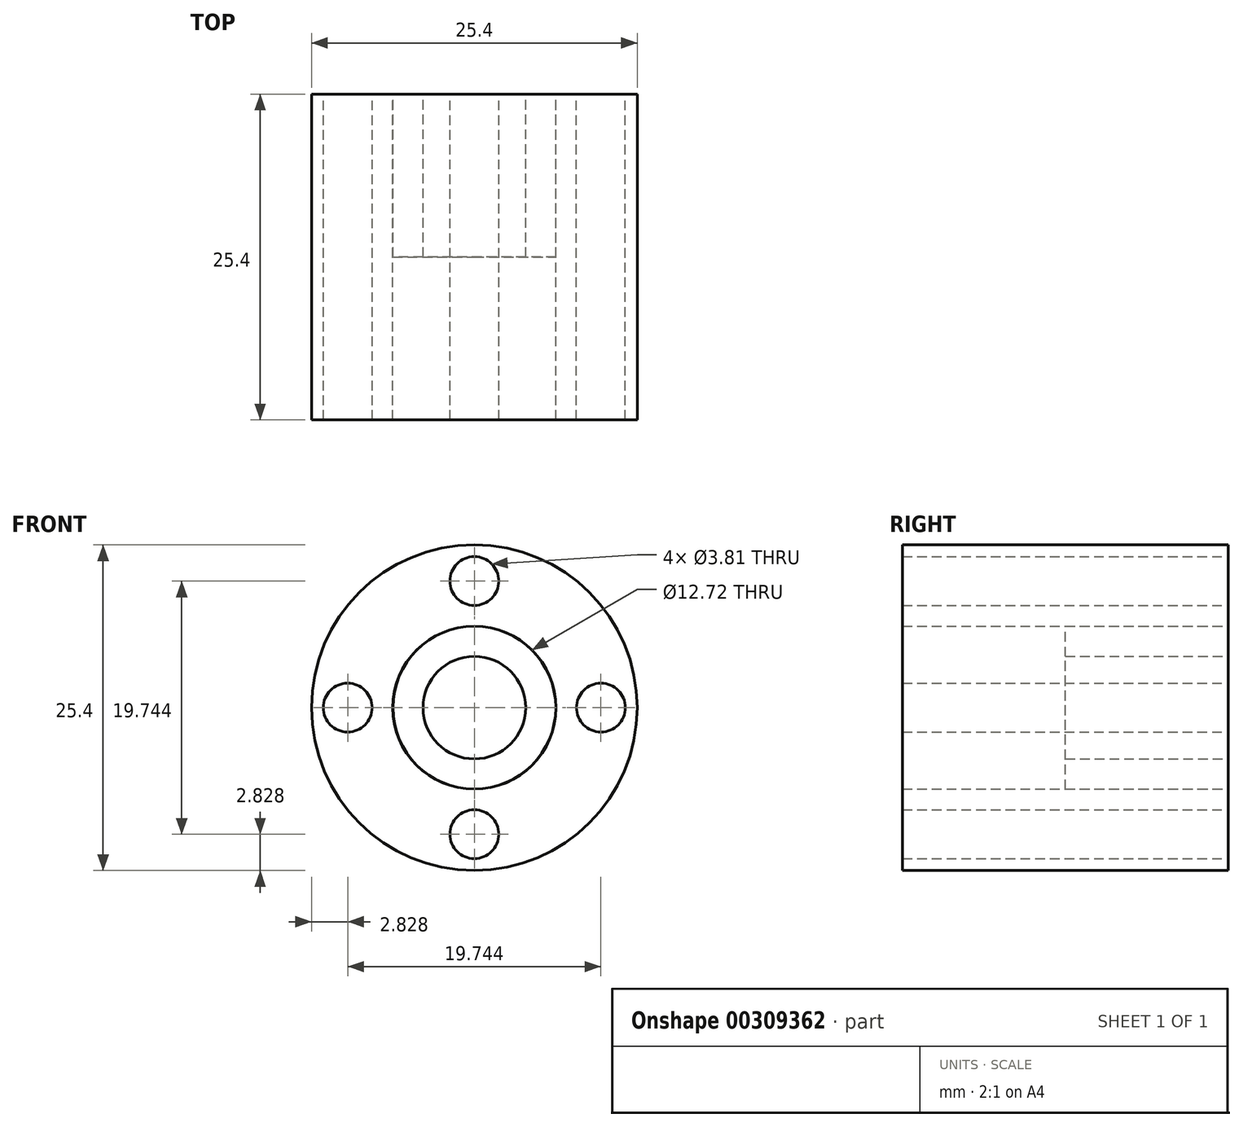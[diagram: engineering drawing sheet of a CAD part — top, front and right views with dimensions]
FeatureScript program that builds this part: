
annotation { "Feature Type Name" : "Feature", "Feature Type Description" : "" }
export const myFeature = defineFeature(function(context is Context, id is Id, definition is map)
    precondition{}
    {
        {
            var Q0;
            Q0=qCreatedBy(makeId("Front.planeOp"),FACE);
            var sketch = newSketch(context, id + "F0", { "sketchPlane" : qUnion([Q0])});
            skCircle(sketch, "E0", {"center": v(0, 0) * mm, "radius": 12.7 * mm});
            skCircle(sketch, "E1", {"center": v(0, 0) * mm, "radius": 6.36 * mm});
            skCircle(sketch, "E2", {"center": v(0, 0) * mm, "radius": 4 * mm});
            skCircle(sketch, "E3", {"center": v(0, 0) * mm, "radius": 6.35 * mm});
            skCircle(sketch, "E4", {"center": v(-9.87, 0) * mm, "radius": 1.9 * mm});
            skCircle(sketch, "E5", {"center": v(0, 9.87) * mm, "radius": 1.9 * mm});
            skCircle(sketch, "E6", {"center": v(9.87, 0) * mm, "radius": 1.9 * mm});
            skCircle(sketch, "E7", {"center": v(0, -9.87) * mm, "radius": 1.9 * mm});
            skSolve(sketch);
        }
        {
            var Q0;
            Q0 = qSketchRegion(id + "F0", true);
            extrude(context, id + "F1", {"entities" : qUnion([Q0]), "depth" : 25.4 * mm});
        }
        {
            var Q0;
            Q0=makeQuery(id+"F0.imprint","IMPRINT",FACE,{"disambiguationData":[TD([[makeQuery(id+"F0.imprint","IMPRINT",EDGE,{"derivedFrom":sQuery(id+"F0.wireOp",EDGE,"E2")}),-1.0]])]});
            extrude(context, id + "F2", {"entities" : qUnion([Q0]), "depth" : 12.7 * mm});
        }
    });
